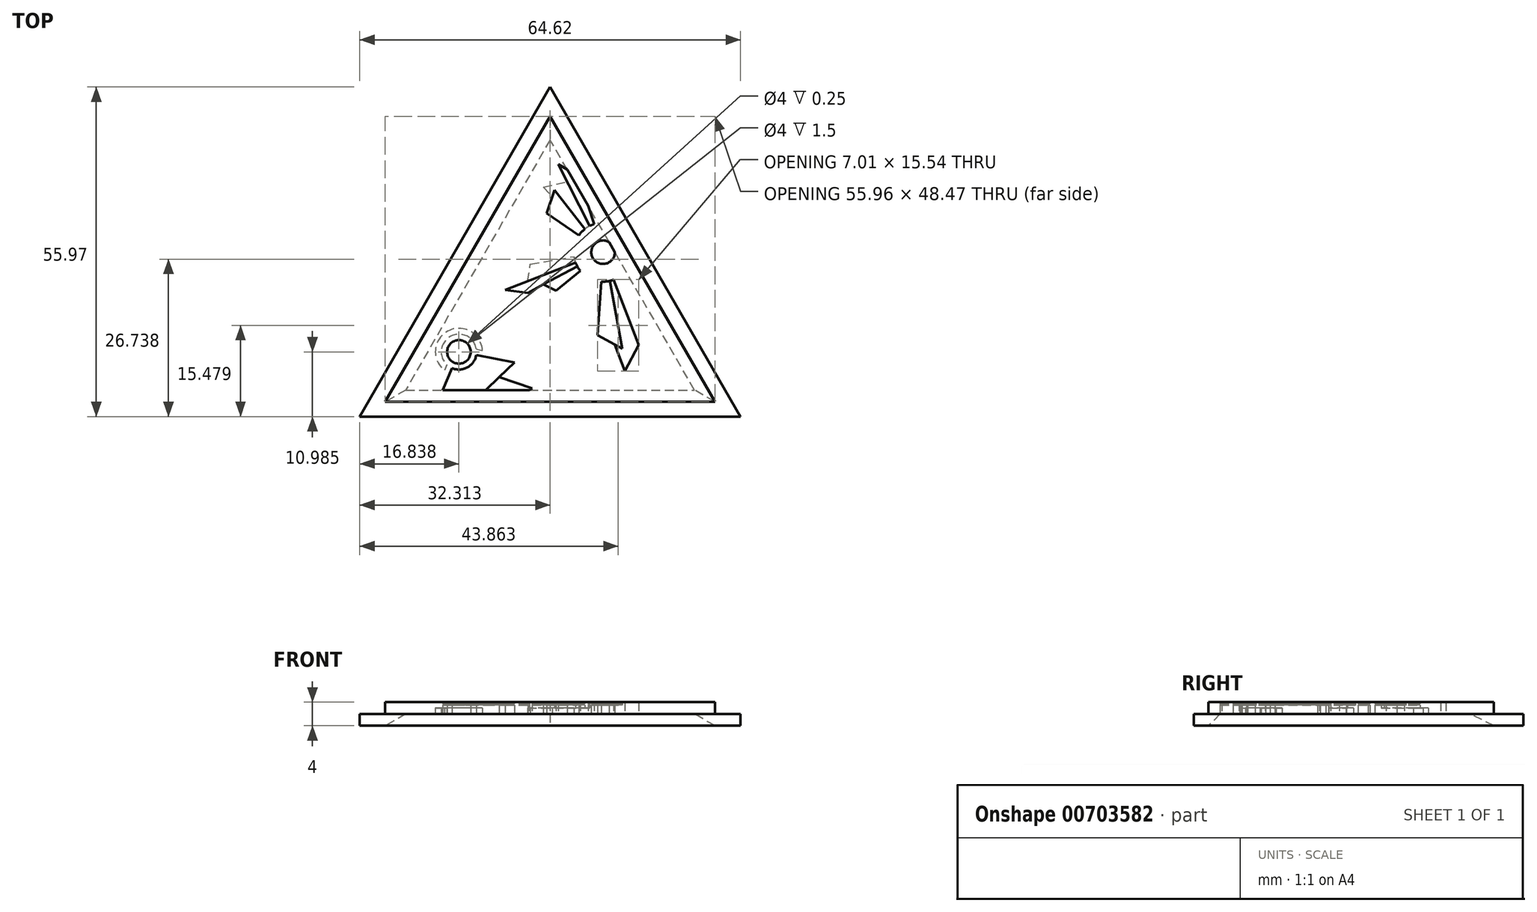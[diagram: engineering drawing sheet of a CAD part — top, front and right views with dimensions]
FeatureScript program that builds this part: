
annotation { "Feature Type Name" : "Feature", "Feature Type Description" : "" }
export const myFeature = defineFeature(function(context is Context, id is Id, definition is map)
    precondition{}
    {
        {
            var Q0;
            Q0=qCreatedBy(makeId("Top.planeOp"),FACE);
            var sketch = newSketch(context, id + "F0", { "sketchPlane" : qUnion([Q0])});
            skLineSegment(sketch, "E0", {"start": v(4.8, 63.3) * mm, "end": v(-23.18, 14.82) * mm});
            skLineSegment(sketch, "E1", {"start": v(-23.18, 14.82) * mm, "end": v(32.78, 14.82) * mm});
            skLineSegment(sketch, "E2", {"start": v(32.78, 14.82) * mm, "end": v(4.8, 63.3) * mm});
            skLineSegment(sketch, "E3", {"start": v(4.8, 68.3) * mm, "end": v(-27.5, 12.32) * mm});
            skLineSegment(sketch, "E4", {"start": v(-27.5, 12.32) * mm, "end": v(37.11, 12.32) * mm});
            skLineSegment(sketch, "E5", {"start": v(37.11, 12.32) * mm, "end": v(4.8, 68.3) * mm});
            skLineSegment(sketch, "E6", {"start": v(4.8, 59.3) * mm, "end": v(-19.72, 16.82) * mm});
            skLineSegment(sketch, "E7", {"start": v(-19.72, 16.82) * mm, "end": v(29.32, 16.82) * mm});
            skLineSegment(sketch, "E8", {"start": v(29.32, 16.82) * mm, "end": v(4.8, 59.3) * mm});
            skSolve(sketch);
        }
        {
            var Q0;
            Q0=makeQuery(id+"F0.imprint","IMPRINT",FACE,{"disambiguationData":[TD([[makeQuery(id+"F0.imprint","IMPRINT",EDGE,{"derivedFrom":sQuery(id+"F0.wireOp",EDGE,"E0")}),1.0]])]});
            extrude(context, id + "F1", {"entities" : qUnion([Q0]), "depth" : 4 * mm, "offsetDistance" : 25 * mm});
        }
        {
            var Q0;
            Q0=makeQuery(id+"F0.imprint","IMPRINT",FACE,{"disambiguationData":[TD([[makeQuery(id+"F0.imprint","IMPRINT",EDGE,{"derivedFrom":sQuery(id+"F0.wireOp",EDGE,"E0")}),-1.0]])]});
            extrude(context, id + "F2", {"entities" : qUnion([Q0]), "operationType" : NewBodyOperationType.ADD, "depth" : 2 * mm, "offsetDistance" : 25 * mm});
        }
        {
            var Q0;
            Q0=makeQuery(id+"F0.imprint","IMPRINT",FACE,{"disambiguationData":[TD([[makeQuery(id+"F0.imprint","IMPRINT",EDGE,{"derivedFrom":sQuery(id+"F0.wireOp",EDGE,"E6")}),1.0]])]});
            extrude(context, id + "F3", {"entities" : qUnion([Q0]), "operationType" : NewBodyOperationType.ADD, "depth" : 4 * mm, "offsetDistance" : 25 * mm, "hasSecondDirection" : true, "secondDirectionOppositeDirection" : true, "secondDirectionDepth" : -2 * mm});
        }
        {
            var Q0;
            Q0=makeQuery(id+"F1.opExtrude","CAP_EDGE",EDGE,{"disambiguationData":[OSD([sQuery(id+"F0.wireOp",EDGE,"E7")])],"isStart":true});
            var Q1;
            Q1=makeQuery(id+"F1.opExtrude","CAP_EDGE",EDGE,{"disambiguationData":[OSD([sQuery(id+"F0.wireOp",EDGE,"E6")])],"isStart":true});
            var Q2;
            Q2=makeQuery(id+"F1.opExtrude","CAP_EDGE",EDGE,{"disambiguationData":[OSD([sQuery(id+"F0.wireOp",EDGE,"E8")])],"isStart":true});
            chamfer(context, id + "F4", {"entities" : qUnion([Q0, Q1, Q2]), "width" : 2 * mm, "tangentPropagation" : true});
        }
        {
            var Q0;
            Q0=makeQuery(id+"F0.imprint","IMPRINT",FACE,{"disambiguationData":[TD([[makeQuery(id+"F0.imprint","IMPRINT",EDGE,{"derivedFrom":sQuery(id+"F0.wireOp",EDGE,"E6")}),1.0]])]});
            var sketch = newSketch(context, id + "F5", { "sketchPlane" : qUnion([Q0])});
            skCircle(sketch, "E9", {"center": v(13.8, 40.23) * mm, "radius": 4 * mm});
            skArc(sketch, "E10", {"start": v(13.46, 35.25) * mm, "mid": v(14.55, 35.29) * mm, "end": v(15.6, 35.57) * mm});
            skLineSegment(sketch, "E11", {"start": v(19.86, 24.49) * mm, "end": v(17.47, 20.03) * mm});
            skLineSegment(sketch, "E12", {"start": v(17.47, 20.03) * mm, "end": v(15.81, 24.55) * mm});
            skLineSegment(sketch, "E13", {"start": v(17.07, 23.88) * mm, "end": v(12.85, 26.14) * mm});
            skLineSegment(sketch, "E14", {"start": v(12.85, 26.14) * mm, "end": v(13.46, 35.25) * mm});
            skLineSegment(sketch, "E15.trimOffspring", {"start": v(14.94, 35.37) * mm, "end": v(17.07, 23.88) * mm});
            skLineSegment(sketch, "E16.trimOffspring", {"start": v(15.6, 35.57) * mm, "end": v(19.86, 24.49) * mm});
            skLineSegment(sketch, "E17", {"start": v(1.05, 33.34) * mm, "end": v(-2.82, 33.81) * mm});
            skLineSegment(sketch, "E18", {"start": v(-2.82, 33.81) * mm, "end": v(9.14, 38.43) * mm});
            skLineSegment(sketch, "E19", {"start": v(1.45, 38.2) * mm, "end": v(1, 35.28) * mm});
            skLineSegment(sketch, "E20.trimOffspring", {"start": v(9.42, 37.82) * mm, "end": v(1.05, 33.34) * mm});
            skLineSegment(sketch, "E21.trimOffspring", {"start": v(8.86, 39.48) * mm, "end": v(1.45, 38.2) * mm});
            skLineSegment(sketch, "E22", {"start": v(9.93, 37.06) * mm, "end": v(5.79, 33.66) * mm});
            skLineSegment(sketch, "E23", {"start": v(5.79, 33.66) * mm, "end": v(3.69, 34.76) * mm});
            skArc(sketch, "E24.trimOffspring", {"start": v(8.86, 39.48) * mm, "mid": v(9.23, 38.2) * mm, "end": v(9.93, 37.06) * mm});
            skCircle(sketch, "E25", {"center": v(13.8, 40.23) * mm, "radius": 2 * mm});
            skLineSegment(sketch, "E26", {"start": v(-18.6, 4.85) * mm, "end": v(-1.22, 21.5) * mm});
            skLineSegment(sketch, "E27", {"start": v(-1.22, 21.5) * mm, "end": v(-7.73, 22.74) * mm});
            skLineSegment(sketch, "E28", {"start": v(-11.86, 20.55) * mm, "end": v(-18.6, 4.85) * mm});
            skPoint(sketch, "E29.end.orphan", {"position": v(-18.6, 4.85) * mm});
            skLineSegment(sketch, "E30", {"start": v(-3.82, 19.01) * mm, "end": v(1.77, 17.12) * mm});
            skLineSegment(sketch, "E31", {"start": v(1.77, 17.12) * mm, "end": v(-18.6, 4.85) * mm});
            skArc(sketch, "E32", {"start": v(-7.7, 23.76) * mm, "mid": v(-12.08, 25.96) * mm, "end": v(-12.7, 21.1) * mm});
            skCircle(sketch, "E33", {"center": v(-10.67, 23.3) * mm, "radius": 2 * mm});
            skCircle(sketch, "E34", {"center": v(13.8, 40.23) * mm, "radius": 5 * mm});
            skLineSegment(sketch, "E35", {"start": v(5.54, 50.76) * mm, "end": v(4.21, 46.81) * mm});
            skLineSegment(sketch, "E36", {"start": v(9.68, 43.06) * mm, "end": v(4.21, 46.81) * mm});
            skLineSegment(sketch, "E37.trimOffspring", {"start": v(10.72, 44.17) * mm, "end": v(5.54, 50.76) * mm});
            skLineSegment(sketch, "E38", {"start": v(6.2, 55.17) * mm, "end": v(11.53, 44.69) * mm});
            skLineSegment(sketch, "E39", {"start": v(6.2, 55.17) * mm, "end": v(9.66, 53.08) * mm});
            skLineSegment(sketch, "E40", {"start": v(9.66, 53.08) * mm, "end": v(12.27, 45) * mm});
            skLineSegment(sketch, "E41", {"start": v(7.72, 52.17) * mm, "end": v(3.64, 51.29) * mm});
            skLineSegment(sketch, "E42.trimOffspring", {"start": v(5.16, 49.63) * mm, "end": v(3.64, 51.29) * mm});
            skArc(sketch, "E43", {"start": v(-6.68, 23.56) * mm, "mid": v(-12.55, 26.84) * mm, "end": v(-13.12, 20.14) * mm});
            skLineSegment(sketch, "E44", {"start": v(-6.68, 23.56) * mm, "end": v(-7.7, 23.76) * mm});
            skLineSegment(sketch, "E45", {"start": v(-13.12, 20.14) * mm, "end": v(-12.7, 21.1) * mm});
            skArc(sketch, "E46.trimOffspring", {"start": v(-11.86, 20.55) * mm, "mid": v(-9.27, 20.66) * mm, "end": v(-7.73, 22.74) * mm});
            skSolve(sketch);
        }
        {
            var Q0;
            {var subQ0=sQuery(id+"F5.wireOp",EDGE,"E25");var subQ1=makeQuery(id+"F0.imprint","IMPRINT",EDGE,{"derivedFrom":sQuery(id+"F0.wireOp",EDGE,"E8")});var subQ2=makeQuery(id+"F5.imprint","INTERSECT",VERTEX,{"disambiguationData":[OD(0.0)],"derivedFrom":[subQ1,subQ0]});Q0=makeQuery(id+"F5.imprint","IMPRINT",FACE,{"disambiguationData":[TD([[makeQuery(id+"F5.imprint","IMPRINT",EDGE,{"disambiguationData":[TD([[subQ2,-1.0]])],"derivedFrom":subQ0}),1.0]])]});}
            var Q1;
            Q1=makeQuery(id+"F5.imprint","IMPRINT",FACE,{"disambiguationData":[TD([[makeQuery(id+"F5.imprint","IMPRINT",EDGE,{"derivedFrom":sQuery(id+"F5.wireOp",EDGE,"E33")}),1.0]])]});
            var Q2;
            {var subQ2=sQuery(id+"F5.wireOp",EDGE,"E14");Q2=makeQuery(id+"F5.imprint","IMPRINT",FACE,{"disambiguationData":[TD([[makeQuery(id+"F5.imprint","IMPRINT",EDGE,{"derivedFrom":subQ2}),-1.0]])]});}
            var Q3;
            {var subQ7=sQuery(id+"F5.wireOp",EDGE,"E17");Q3=makeQuery(id+"F5.imprint","IMPRINT",FACE,{"disambiguationData":[TD([[makeQuery(id+"F5.imprint","IMPRINT",EDGE,{"derivedFrom":subQ7}),-1.0]])]});}
            var Q4;
            {var subQ0=sQuery(id+"F5.wireOp",EDGE,"E36");Q4=makeQuery(id+"F5.imprint","IMPRINT",FACE,{"disambiguationData":[TD([[makeQuery(id+"F5.imprint","IMPRINT",EDGE,{"derivedFrom":subQ0}),-1.0]])]});}
            var Q5;
            {var subQ4=sQuery(id+"F5.wireOp",EDGE,"E27");Q5=makeQuery(id+"F5.imprint","IMPRINT",FACE,{"disambiguationData":[TD([[makeQuery(id+"F5.imprint","IMPRINT",EDGE,{"derivedFrom":subQ4}),1.0]])]});}
            extrude(context, id + "F6", {"entities" : qUnion([Q0, Q1, Q2, Q3, Q4, Q5]), "operationType" : NewBodyOperationType.REMOVE, "oppositeDirection" : true, "depth" : -4 * mm, "offsetDistance" : 25 * mm, "hasSecondDirection" : true, "secondDirectionOppositeDirection" : true, "secondDirectionDepth" : -3.75 * mm});
        }
        {
            var Q0;
            {var subQ0=sQuery(id+"F5.wireOp",EDGE,"E25");var subQ1=makeQuery(id+"F0.imprint","IMPRINT",EDGE,{"derivedFrom":sQuery(id+"F0.wireOp",EDGE,"E8")});var subQ2=makeQuery(id+"F5.imprint","INTERSECT",VERTEX,{"disambiguationData":[OD(0.0)],"derivedFrom":[subQ1,subQ0]});Q0=makeQuery(id+"F5.imprint","IMPRINT",FACE,{"disambiguationData":[TD([[makeQuery(id+"F5.imprint","IMPRINT",EDGE,{"disambiguationData":[TD([[subQ2,-1.0]])],"derivedFrom":subQ0}),1.0]])]});}
            var Q1;
            Q1=makeQuery(id+"F5.imprint","IMPRINT",FACE,{"disambiguationData":[TD([[makeQuery(id+"F5.imprint","IMPRINT",EDGE,{"derivedFrom":sQuery(id+"F5.wireOp",EDGE,"E33")}),1.0]])]});
            extrude(context, id + "F7", {"entities" : qUnion([Q0, Q1]), "operationType" : NewBodyOperationType.REMOVE, "depth" : 3.5 * mm, "offsetDistance" : 25 * mm});
        }
        {
            var Q0;
            {var subQ7=sQuery(id+"F5.wireOp",EDGE,"E17");Q0=makeQuery(id+"F5.imprint","IMPRINT",FACE,{"disambiguationData":[TD([[makeQuery(id+"F5.imprint","IMPRINT",EDGE,{"derivedFrom":subQ7}),-1.0]])]});}
            var Q1;
            {var subQ0=sQuery(id+"F5.wireOp",EDGE,"E14");Q1=makeQuery(id+"F5.imprint","IMPRINT",FACE,{"disambiguationData":[TD([[makeQuery(id+"F5.imprint","IMPRINT",EDGE,{"derivedFrom":subQ0}),-1.0]])]});}
            var Q2;
            {var subQ5=sQuery(id+"F5.wireOp",EDGE,"E27");Q2=makeQuery(id+"F5.imprint","IMPRINT",FACE,{"disambiguationData":[TD([[makeQuery(id+"F5.imprint","IMPRINT",EDGE,{"derivedFrom":subQ5}),1.0]])]});}
            var Q3;
            {var subQ0=sQuery(id+"F5.wireOp",EDGE,"E36");Q3=makeQuery(id+"F5.imprint","IMPRINT",FACE,{"disambiguationData":[TD([[makeQuery(id+"F5.imprint","IMPRINT",EDGE,{"derivedFrom":subQ0}),-1.0]])]});}
            extrude(context, id + "F8", {"entities" : qUnion([Q0, Q1, Q2, Q3]), "operationType" : NewBodyOperationType.REMOVE, "oppositeDirection" : true, "depth" : -3.5 * mm, "offsetDistance" : 25 * mm});
        }
        {
            var Q0;
            Q0=makeQuery(id+"F5.imprint","IMPRINT",FACE,{"disambiguationData":[TD([[makeQuery(id+"F5.imprint","IMPRINT",EDGE,{"derivedFrom":sQuery(id+"F5.wireOp",EDGE,"E11")}),-1.0]])]});
            var Q1;
            {var subQ0=sQuery(id+"F5.wireOp",EDGE,"E30");Q1=makeQuery(id+"F5.imprint","IMPRINT",FACE,{"disambiguationData":[TD([[makeQuery(id+"F5.imprint","IMPRINT",EDGE,{"derivedFrom":subQ0}),-1.0]])]});}
            var Q2;
            {var subQ4=sQuery(id+"F5.wireOp",EDGE,"E22");Q2=makeQuery(id+"F5.imprint","IMPRINT",FACE,{"disambiguationData":[TD([[makeQuery(id+"F5.imprint","IMPRINT",EDGE,{"derivedFrom":subQ4}),-1.0]])]});}
            var Q3;
            {var subQ1=sQuery(id+"F5.wireOp",EDGE,"E38");var subQ5=sQuery(id+"F5.wireOp",EDGE,"E34");var subQ6=makeQuery(id+"F5.imprint","INTERSECT",VERTEX,{"derivedFrom":[subQ5,subQ1]});Q3=makeQuery(id+"F5.imprint","IMPRINT",FACE,{"disambiguationData":[TD([[makeQuery(id+"F5.imprint","IMPRINT",EDGE,{"disambiguationData":[TD([[subQ6,1.0]])],"derivedFrom":subQ5}),-1.0]])]});}
            var Q4;
            Q4=makeQuery(id+"F5.imprint","IMPRINT",FACE,{"disambiguationData":[TD([[makeQuery(id+"F5.imprint","IMPRINT",EDGE,{"derivedFrom":sQuery(id+"F5.wireOp",EDGE,"E32")}),-1.0]])]});
            extrude(context, id + "F9", {"entities" : qUnion([Q0, Q1, Q2, Q3, Q4]), "operationType" : NewBodyOperationType.REMOVE, "oppositeDirection" : true, "depth" : -3 * mm, "offsetDistance" : 25 * mm});
        }
        {
            var Q0;
            Q0=makeQuery(id+"F9.boolean.opBoolean","COPY",FACE,{"derivedFrom":makeQuery(id+"F9.opExtrude","CAP_FACE",FACE,{"disambiguationData":[OSD([sQuery(id+"F0.wireOp",EDGE,"E8"),sQuery(id+"F5.wireOp",EDGE,"E34"),sQuery(id+"F5.wireOp",EDGE,"E38"),sQuery(id+"F5.wireOp",EDGE,"E39"),sQuery(id+"F5.wireOp",EDGE,"E40")])],"isStart":false})});
            var Q1;
            Q1=makeQuery(id+"F9.boolean.opBoolean","COPY",FACE,{"derivedFrom":makeQuery(id+"F9.opExtrude","CAP_FACE",FACE,{"disambiguationData":[OSD([sQuery(id+"F5.wireOp",EDGE,"E20.trimOffspring"),sQuery(id+"F5.wireOp",EDGE,"E22"),sQuery(id+"F5.wireOp",EDGE,"E23"),sQuery(id+"F5.wireOp",EDGE,"E34")])],"isStart":false})});
            var Q2;
            Q2=makeQuery(id+"F9.boolean.opBoolean","COPY",FACE,{"derivedFrom":makeQuery(id+"F9.opExtrude","CAP_FACE",FACE,{"disambiguationData":[OSD([sQuery(id+"F0.wireOp",EDGE,"E7"),sQuery(id+"F5.wireOp",EDGE,"E26"),sQuery(id+"F5.wireOp",EDGE,"E30"),sQuery(id+"F5.wireOp",EDGE,"E31")])],"isStart":false})});
            var Q3;
            Q3=makeQuery(id+"F9.boolean.opBoolean","COPY",FACE,{"derivedFrom":makeQuery(id+"F9.opExtrude","CAP_FACE",FACE,{"disambiguationData":[OSD([sQuery(id+"F5.wireOp",EDGE,"E11"),sQuery(id+"F5.wireOp",EDGE,"E12"),sQuery(id+"F5.wireOp",EDGE,"E13"),sQuery(id+"F5.wireOp",EDGE,"E15.trimOffspring"),sQuery(id+"F5.wireOp",EDGE,"E16.trimOffspring"),sQuery(id+"F5.wireOp",EDGE,"E34")])],"isStart":false})});
            extrude(context, id + "F10", {"entities" : qUnion([Q0, Q1, Q2, Q3]), "operationType" : NewBodyOperationType.REMOVE, "oppositeDirection" : true, "depth" : 3.25 * mm, "offsetDistance" : 25 * mm});
        }
        {
            var Q0;
            {var subQ3=sQuery(id+"F5.wireOp",EDGE,"E19");Q0=makeQuery(id+"F5.imprint","IMPRINT",FACE,{"disambiguationData":[TD([[makeQuery(id+"F5.imprint","IMPRINT",EDGE,{"derivedFrom":subQ3}),1.0]])]});}
            var Q1;
            {var subQ0=sQuery(id+"F5.wireOp",EDGE,"E37.trimOffspring");Q1=makeQuery(id+"F5.imprint","IMPRINT",FACE,{"disambiguationData":[TD([[makeQuery(id+"F5.imprint","IMPRINT",EDGE,{"derivedFrom":subQ0}),-1.0]])]});}
            extrude(context, id + "F11", {"entities" : qUnion([Q0, Q1]), "operationType" : NewBodyOperationType.REMOVE, "depth" : 3 * mm, "offsetDistance" : 25 * mm});
        }
    });
